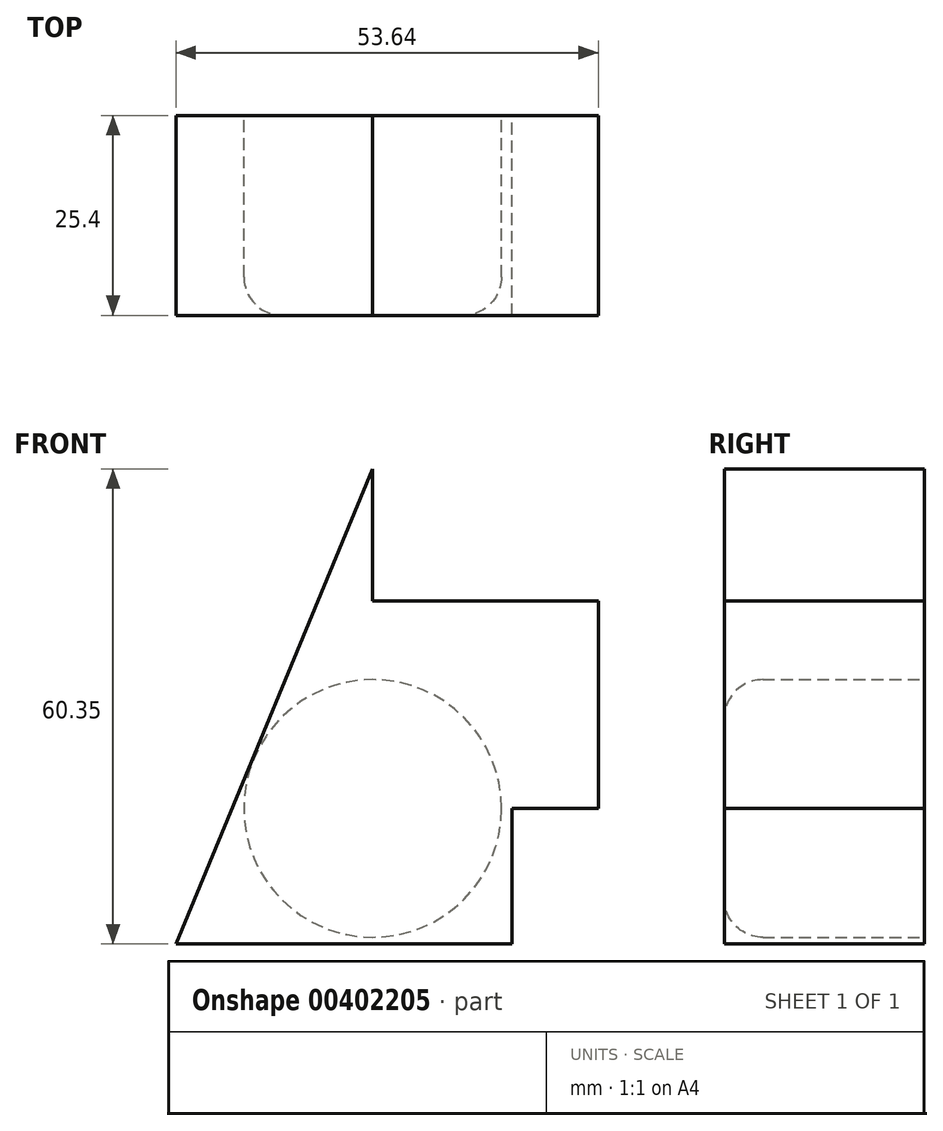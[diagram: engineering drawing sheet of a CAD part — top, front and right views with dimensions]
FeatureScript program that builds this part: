
annotation { "Feature Type Name" : "Feature", "Feature Type Description" : "" }
export const myFeature = defineFeature(function(context is Context, id is Id, definition is map)
    precondition{}
    {
        {
            var Q0;
            Q0=qCreatedBy(makeId("Front.planeOp"),FACE);
            var sketch = newSketch(context, id + "F0", { "sketchPlane" : qUnion([Q0])});
            skLineSegment(sketch, "E0", {"start": v(-25, -17.22) * mm, "end": v(27.43, -17.22) * mm});
            skLineSegment(sketch, "E1", {"start": v(-25, -17.22) * mm, "end": v(0, 43.13) * mm});
            skLineSegment(sketch, "E2", {"start": v(0, 43.13) * mm, "end": v(28.65, 43.13) * mm});
            skLineSegment(sketch, "E3", {"start": v(28.65, 43.13) * mm, "end": v(28.65, -17.22) * mm});
            skCircle(sketch, "E4", {"center": v(0, 0) * mm, "radius": 16.36 * mm});
            skLineSegment(sketch, "E5.bottom", {"start": v(28.65, 43.13) * mm, "end": v(0, 43.13) * mm});
            skLineSegment(sketch, "E5.top", {"start": v(28.65, 26.37) * mm, "end": v(0, 26.37) * mm});
            skLineSegment(sketch, "E5.left", {"start": v(28.65, 43.13) * mm, "end": v(28.65, 26.37) * mm});
            skLineSegment(sketch, "E5.right", {"start": v(0, 43.13) * mm, "end": v(0, 26.37) * mm});
            skLineSegment(sketch, "E6", {"start": v(0, 26.37) * mm, "end": v(-6.94, 26.37) * mm});
            skLineSegment(sketch, "E7", {"start": v(0, 34.75) * mm, "end": v(0, 43.13) * mm});
            skLineSegment(sketch, "E8", {"start": v(28.65, 26.37) * mm, "end": v(17.71, 0) * mm});
            skLineSegment(sketch, "E9", {"start": v(17.71, 0) * mm, "end": v(6.77, 26.37) * mm});
            skLineSegment(sketch, "E10", {"start": v(6.77, 26.37) * mm, "end": v(-12.5, 12.95) * mm});
            skLineSegment(sketch, "E11", {"start": v(-12.5, 12.95) * mm, "end": v(6.77, 26.37) * mm});
            skLineSegment(sketch, "E12", {"start": v(17.71, 0) * mm, "end": v(28.65, 0) * mm});
            skLineSegment(sketch, "E13", {"start": v(17.71, 0) * mm, "end": v(17.71, -17.22) * mm});
            skLineSegment(sketch, "E14", {"start": v(17.71, -17.22) * mm, "end": v(27.43, -17.22) * mm});
            skSolve(sketch);
        }
        {
            var Q0;
            Q0=makeQuery(id+"F0.imprint","IMPRINT",FACE,{"disambiguationData":[TD([[makeQuery(id+"F0.imprint","IMPRINT",EDGE,{"derivedFrom":sQuery(id+"F0.wireOp",EDGE,"E5.bottom")}),1.0]])]});
            var Q1;
            Q1=makeQuery(id+"F0.imprint","IMPRINT",FACE,{"disambiguationData":[TD([[makeQuery(id+"F0.imprint","IMPRINT",EDGE,{"derivedFrom":sQuery(id+"F0.wireOp",EDGE,"E4")}),1.0]])]});
            extrude(context, id + "F1", {"entities" : qUnion([Q0, Q1]), "depth" : 25.4 * mm});
        }
        {
            var Q0;
            Q0=makeQuery(id+"F0.imprint","IMPRINT",FACE,{"disambiguationData":[TD([[makeQuery(id+"F0.imprint","IMPRINT",EDGE,{"derivedFrom":sQuery(id+"F0.wireOp",EDGE,"E5.bottom")}),1.0]])]});
            var Q1;
            Q1=makeQuery(id+"F0.imprint","IMPRINT",FACE,{"disambiguationData":[TD([[makeQuery(id+"F0.imprint","IMPRINT",EDGE,{"derivedFrom":sQuery(id+"F0.wireOp",EDGE,"E5.right")}),-1.0]])]});
            var Q2;
            {var subQ0=sQuery(id+"F0.wireOp",EDGE,"E6");Q2=makeQuery(id+"F0.imprint","IMPRINT",FACE,{"disambiguationData":[TD([[makeQuery(id+"F0.imprint","IMPRINT",EDGE,{"derivedFrom":subQ0}),1.0]])]});}
            var Q3;
            {var subQ0=sQuery(id+"F0.wireOp",EDGE,"E8");Q3=makeQuery(id+"F0.imprint","IMPRINT",FACE,{"disambiguationData":[TD([[makeQuery(id+"F0.imprint","IMPRINT",EDGE,{"derivedFrom":subQ0}),-1.0]])]});}
            var Q4;
            {var subQ0=sQuery(id+"F0.wireOp",EDGE,"E8");Q4=makeQuery(id+"F0.imprint","IMPRINT",FACE,{"disambiguationData":[TD([[makeQuery(id+"F0.imprint","IMPRINT",EDGE,{"derivedFrom":subQ0}),1.0]])]});}
            var Q5;
            {var subQ5=sQuery(id+"F0.wireOp",EDGE,"E0");Q5=makeQuery(id+"F0.imprint","IMPRINT",FACE,{"disambiguationData":[TD([[makeQuery(id+"F0.imprint","IMPRINT",EDGE,{"derivedFrom":subQ5}),1.0]])]});}
            var Q6;
            Q6=makeQuery(id+"F0.imprint","IMPRINT",FACE,{"disambiguationData":[TD([[makeQuery(id+"F0.imprint","IMPRINT",EDGE,{"derivedFrom":sQuery(id+"F0.wireOp",EDGE,"E4")}),1.0]])]});
            extrude(context, id + "F2", {"entities" : qUnion([Q0, Q1, Q2, Q3, Q4, Q5, Q6]), "depth" : 25.4 * mm});
        }
        {
            var Q0;
            Q0=makeQuery(id+"F1.opExtrude","CAP_FACE",FACE,{"disambiguationData":[OSD([sQuery(id+"F0.wireOp",EDGE,"E5.bottom"),sQuery(id+"F0.wireOp",EDGE,"E5.top"),sQuery(id+"F0.wireOp",EDGE,"E5.left"),sQuery(id+"F0.wireOp",EDGE,"E5.right"),sQuery(id+"F0.wireOp",EDGE,"E7")])],"isStart":false});
            var Q1;
            Q1=makeQuery(id+"F2.opExtrude","CAP_FACE",FACE,{"disambiguationData":[OSD([sQuery(id+"F0.wireOp",EDGE,"E0"),sQuery(id+"F0.wireOp",EDGE,"E1"),sQuery(id+"F0.wireOp",EDGE,"E3"),sQuery(id+"F0.wireOp",EDGE,"E5.bottom"),sQuery(id+"F0.wireOp",EDGE,"E5.left"),sQuery(id+"F0.wireOp",EDGE,"E12"),sQuery(id+"F0.wireOp",EDGE,"E13")])],"isStart":false});
            var Q2;
            Q2=makeQuery(id+"F1.opExtrude","CAP_FACE",FACE,{"disambiguationData":[OSD([sQuery(id+"F0.wireOp",EDGE,"E4")])],"isStart":false});
            fillet(context, id + "F3", {"entities" : qUnion([Q0, Q1, Q2]), "radius" : 4.9 * mm, "tangentPropagation" : true, "allowEdgeOverflow" : false});
        }
    });
